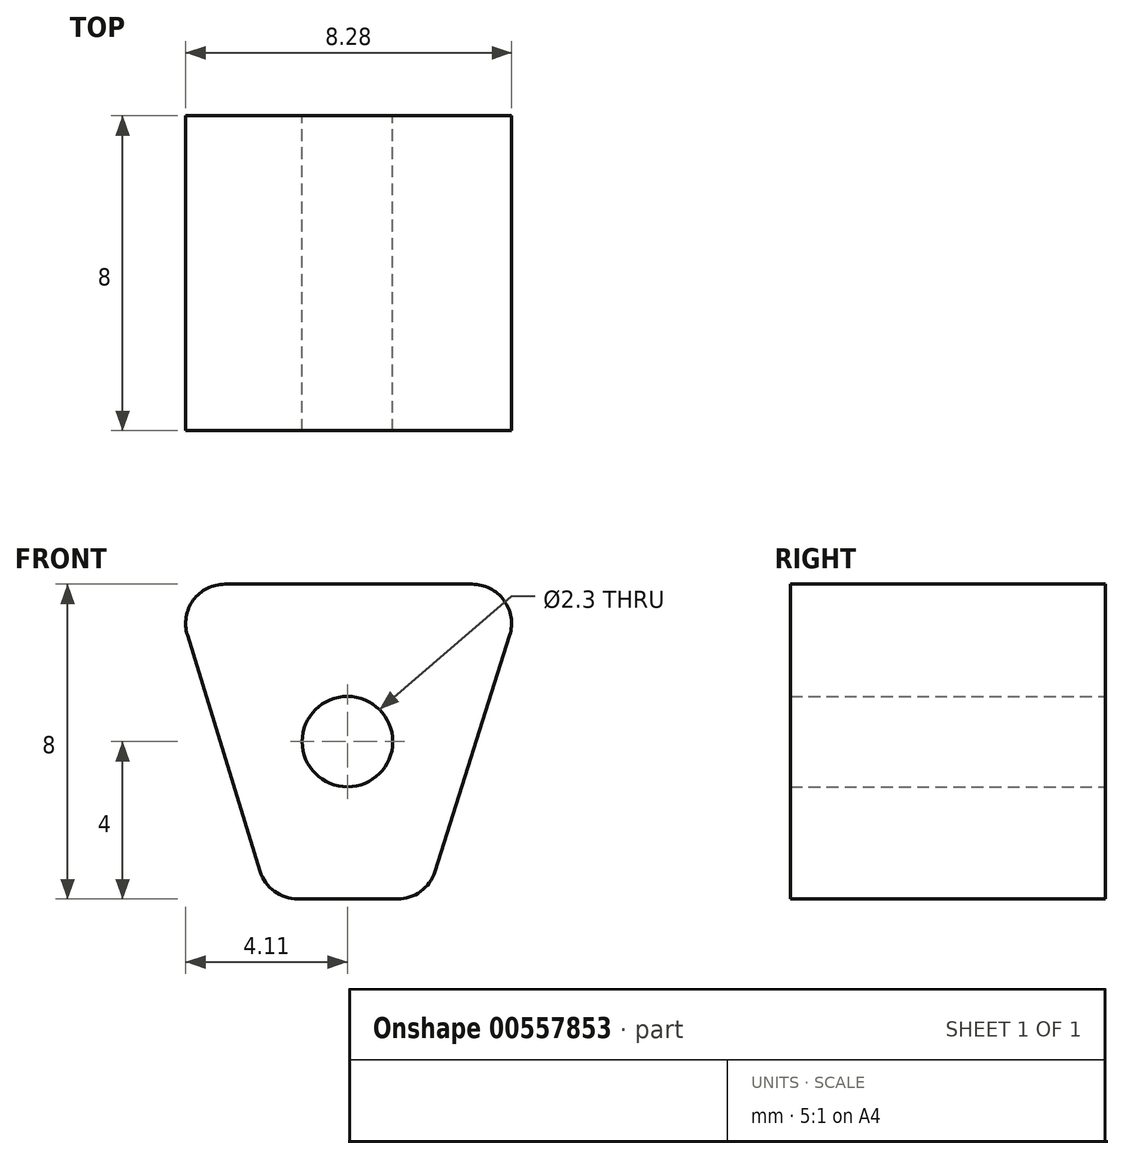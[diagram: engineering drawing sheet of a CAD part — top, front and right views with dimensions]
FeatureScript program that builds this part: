
annotation { "Feature Type Name" : "Feature", "Feature Type Description" : "" }
export const myFeature = defineFeature(function(context is Context, id is Id, definition is map)
    precondition{}
    {
        {
            var Q0;
            Q0=qCreatedBy(makeId("Front.planeOp"),FACE);
            var sketch = newSketch(context, id + "F0", { "sketchPlane" : qUnion([Q0])});
            skLineSegment(sketch, "E0", {"start": v(-3.11, 0) * mm, "end": v(3.17, 0) * mm});
            skLineSegment(sketch, "E1", {"start": v(0, 0) * mm, "end": v(0, -8) * mm, "construction": true});
            skCircle(sketch, "E2", {"center": v(0, -4) * mm, "radius": 1.15 * mm});
            skLineSegment(sketch, "E3", {"start": v(-1.26, -8) * mm, "end": v(1.27, -8) * mm});
            skPoint(sketch, "E4", {"position": v(0, -8) * mm});
            skLineSegment(sketch, "E5", {"start": v(-4.07, -1.3) * mm, "end": v(-2.22, -7.3) * mm});
            skLineSegment(sketch, "E6", {"start": v(4.12, -1.3) * mm, "end": v(2.22, -7.3) * mm});
            skPoint(sketch, "E7.visualSharp", {"position": v(-4.47, 0) * mm});
            skArc(sketch, "E7.filletArc", {"start": v(-3.11, 0) * mm, "mid": v(-3.92, -0.4) * mm, "end": v(-4.07, -1.3) * mm});
            skPoint(sketch, "E8.visualSharp", {"position": v(4.53, 0) * mm});
            skArc(sketch, "E8.filletArc", {"start": v(4.12, -1.3) * mm, "mid": v(3.97, -0.4) * mm, "end": v(3.17, 0) * mm});
            skPoint(sketch, "E9.visualSharp", {"position": v(2, -8) * mm});
            skArc(sketch, "E9.filletArc", {"start": v(1.27, -8) * mm, "mid": v(1.86, -7.8) * mm, "end": v(2.22, -7.3) * mm});
            skPoint(sketch, "E10.visualSharp", {"position": v(-2, -8) * mm});
            skArc(sketch, "E10.filletArc", {"start": v(-2.22, -7.3) * mm, "mid": v(-1.86, -7.8) * mm, "end": v(-1.26, -8) * mm});
            skSolve(sketch);
        }
        {
            var Q0;
            Q0 = qSketchRegion(id + "F0", true);
            extrude(context, id + "F1", {"entities" : qUnion([Q0]), "depth" : 8 * mm, "offsetDistance" : 25 * mm});
        }
    });
